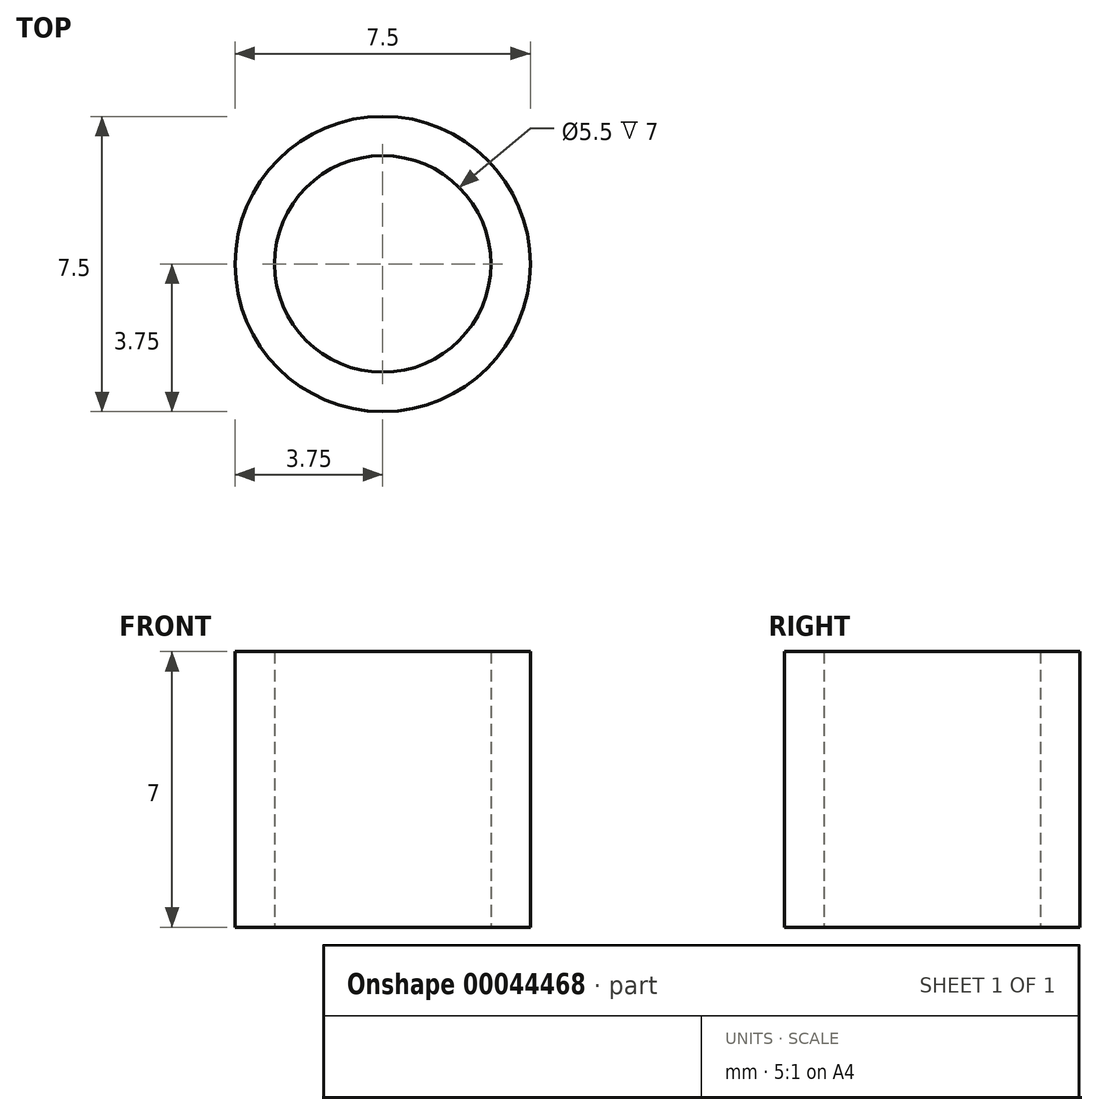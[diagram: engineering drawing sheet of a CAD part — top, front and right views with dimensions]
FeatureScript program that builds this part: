
annotation { "Feature Type Name" : "Feature", "Feature Type Description" : "" }
export const myFeature = defineFeature(function(context is Context, id is Id, definition is map)
    precondition{}
    {
        {
            var Q0;
            Q0=qCreatedBy(makeId("Top.planeOp"),FACE);
            var sketch = newSketch(context, id + "F0", { "sketchPlane" : qUnion([Q0])});
            skCircle(sketch, "E0", {"center": v(0, 0) * mm, "radius": 2.75 * mm});
            skCircle(sketch, "E1", {"center": v(0, 0) * mm, "radius": 3.75 * mm});
            skSolve(sketch);
        }
        {
            var Q0;
            Q0=makeQuery(id+"F0.imprint","IMPRINT",FACE,{"disambiguationData":[TD([[makeQuery(id+"F0.imprint","IMPRINT",EDGE,{"derivedFrom":sQuery(id+"F0.wireOp",EDGE,"E0")}),-1.0]])]});
            extrude(context, id + "F1", {"entities" : qUnion([Q0]), "depth" : 7 * mm});
        }
    });
